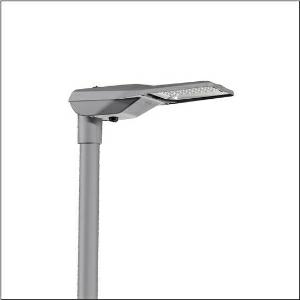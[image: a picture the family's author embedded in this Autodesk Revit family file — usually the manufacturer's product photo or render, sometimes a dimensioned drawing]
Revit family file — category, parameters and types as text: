
# Revit family: streetlight_sl_21_mini___st0_5a_5xe2b43t08jb_6bf0
name_source: partatom
category: Lighting Fixtures
units: mm (PartAtom-declared; Revit-internal decimal feet)

## family parameters
Cut with Voids When Loaded = No
Host = Face
Light Source = No
Part Type = Normal
Room Calculation Point = No
Round Connector Dimension = Use Diameter
Shared = No

## types (1)
- --- (1 x LED, 13500 lm, 88.6 W, 4000K)
    Apparent Load = 89 VA
    CIE Flux Codes = 43 76 97 100 100
    Color Rendering = 70
    Color Temperature = 4000K
    Default Elevation = 1800 mm
    Description = Streetlight SL 21 mini, mast luminaire, primary light control with lens, of PMMA, primary optical cover: cover, of toughened safety glass, transparent, light distribution: ST0.5a, light emission: direct distribution, primary light characteristic: asymmetric, installation type: side-entry, post-top, LED, High Power LED, rated luminous flux: 13.500lm, luminous efficacy: 152lm/W, light colour: 740, colour temperature: 4000K, control gear: D4i, control: overheat protection, constant luminous flux control, time-dependent luminous flux control, flexible luminous flux parameterisation, pre-setting: logarithmic dimming characteristic, mains connection: 220..240V, AC, 50/60Hz, start of lifetime: 89W, end of service life: 92W, reduction: 41W, luminaire housing, of diecast aluminium, powder-coated, SITECO metallic grey (DB 702S), corrosivity category C5 high according to DIN EN ISO 12944, please order mast flange separately, inclination adjustable: 0°, 5°, 10°, 15°, sealing non-destructively replaceable, multi-level sealing system, length: 628mm, width: 235mm, height: 110mm, mast flange for spigot size: 42mm (side-entry): 5XC10008XM4, 60/48mm (side-entry/post-top): 5XC10108XM2, 76/60mm (side-entry/post-top): 5XC10108XM1, mounting height: 4..8m, Smart Interface below and above, protection rating (complete): IP66, insulation class (complete): insulation class II (safety insulation), certification: CE, ENEC, ENEC+, VDE, impact resistance: IK10, permissible operating ambient temperature for outdoor applications: -40..+50°C, standard-compliant lighting for roads and squares, packaging unit: 1 piece

Light Distribution: ST0.5a
    Height = 110 mm
    Lamp = 1 x LED
    Lamp Light Flux = 13500 lm
    Lamp Power = 88.6 W
    Lamp count = 1
    Length = 625 mm
    Luminous efficacy = 152 lm/W
    Manufacturer = Siteco
    ModVariant = No
    Model = 5XE2B43T08JB
    Number of Poles = 1
    OnlyDefault = Yes
    Power Factor = 1
    Product Name = Streetlight SL 21 mini | ST0.5a
    Product group = mast luminaire | pylon top
    ProductGroupID = 6100
    Protection Class = Protection class II
    Protection Degree = IP 66
    RLX_Detail_Level = 1
    RLX_Emergency_Light_Flux = 0 lm
    RLX_Emergency_Type = 0
    RLX_Emergency_Type_DB = No
    RlxData = <blob elided: 37621 chars, md5=579c2109>
    Socket = socket
    Standby Power = 0 W
    System Light Flux = 13500 lm
    System Power = 89 W
    Type Comments = factory setting: luminous flux: 100 % | dim-lin: 254 | 915 mA
    Type Image = l_1003514.jpg
    URL = http://relux.com
    VarID = @adj_031995
    Voltage = 0 V
    Weight = 0.00 kg
    Width = 234 mm

## geometry (parser evidence)
native form markers: Blend x4, Sweep x11
no freeform markers — native parametric forms only
